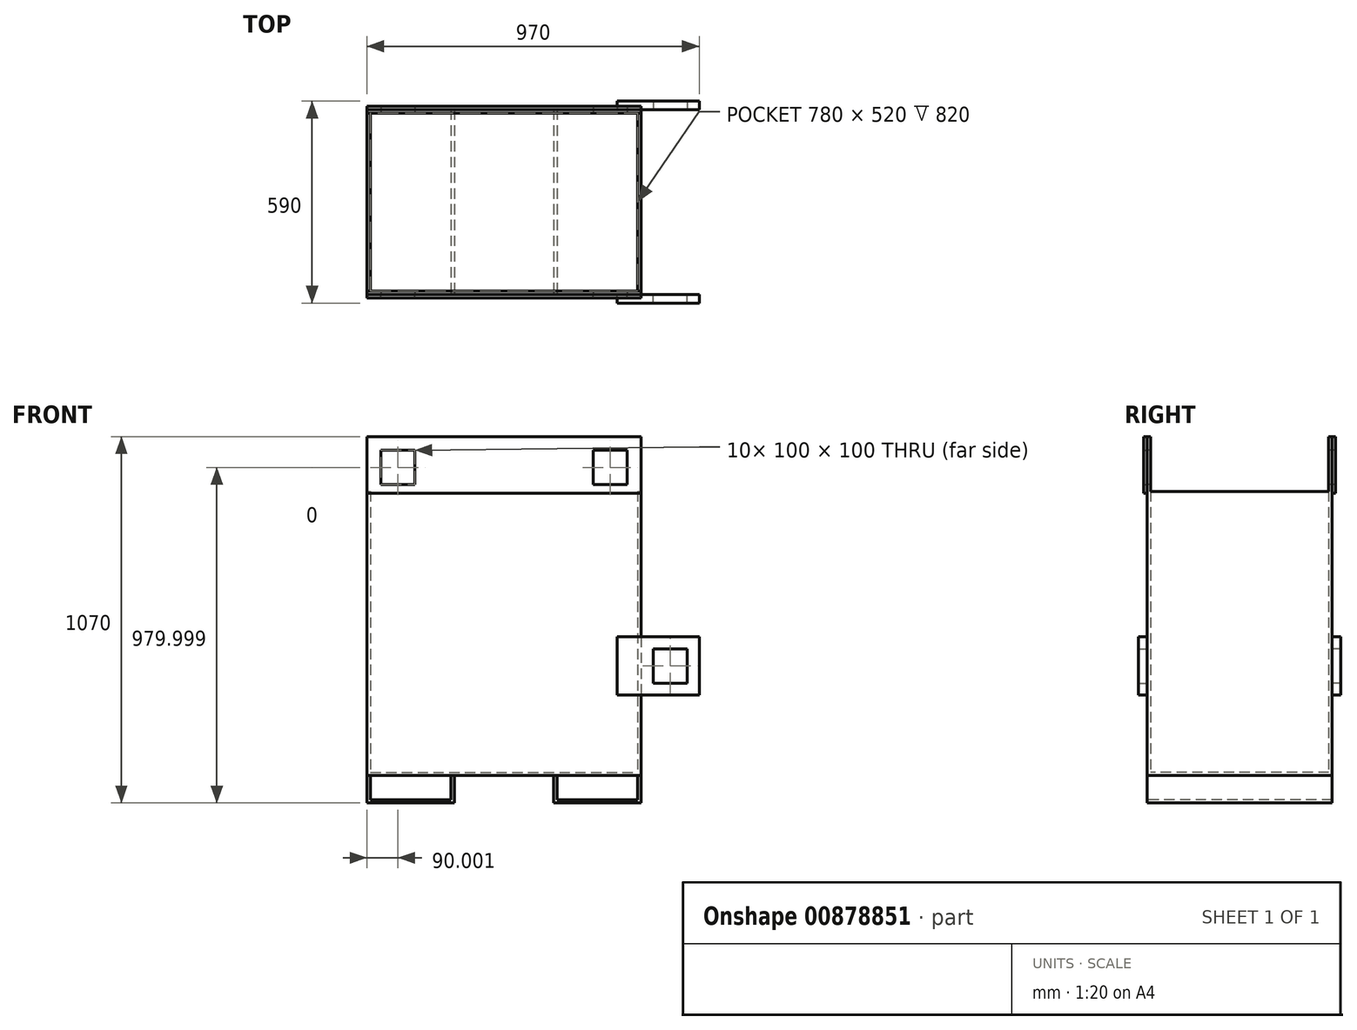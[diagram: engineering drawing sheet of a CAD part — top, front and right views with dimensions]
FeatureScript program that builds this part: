
annotation { "Feature Type Name" : "Feature", "Feature Type Description" : "" }
export const myFeature = defineFeature(function(context is Context, id is Id, definition is map)
    precondition{}
    {
        {
            var Q0;
            Q0=qCreatedBy(makeId("Front.planeOp"),FACE);
            var sketch = newSketch(context, id + "F0", { "sketchPlane" : qUnion([Q0])});
            skLineSegment(sketch, "E0.bottom", {"start": v(-449.14, -487.23) * mm, "end": v(350.86, -487.23) * mm});
            skLineSegment(sketch, "E0.top", {"start": v(-449.14, -497.23) * mm, "end": v(350.86, -497.23) * mm});
            skLineSegment(sketch, "E0.left", {"start": v(-449.14, -487.23) * mm, "end": v(-449.14, -497.23) * mm});
            skLineSegment(sketch, "E0.right", {"start": v(350.86, -487.23) * mm, "end": v(350.86, -497.23) * mm});
            skSolve(sketch);
        }
        {
            var Q0;
            Q0=makeQuery(id+"F0.imprint","IMPRINT",FACE,{"disambiguationData":[TD([[makeQuery(id+"F0.imprint","IMPRINT",EDGE,{"derivedFrom":sQuery(id+"F0.wireOp",EDGE,"E0.bottom")}),-1.0]])]});
            extrude(context, id + "F1", {"entities" : qUnion([Q0]), "depth" : 540 * mm, "offsetDistance" : 25 * mm});
        }
        {
            var Q0;
            Q0=makeQuery(id+"F1.opExtrude","SWEPT_FACE",FACE,{"disambiguationData":[OSD([sQuery(id+"F0.wireOp",EDGE,"E0.bottom")])]});
            var sketch = newSketch(context, id + "F2", { "sketchPlane" : qUnion([Q0])});
            skLineSegment(sketch, "E1.bottom", {"start": v(-439.14, -10) * mm, "end": v(340.86, -10) * mm});
            skLineSegment(sketch, "E1.top", {"start": v(-439.14, -530) * mm, "end": v(340.86, -530) * mm});
            skLineSegment(sketch, "E1.left", {"start": v(-439.14, -10) * mm, "end": v(-439.14, -530) * mm});
            skLineSegment(sketch, "E1.right", {"start": v(340.86, -10) * mm, "end": v(340.86, -530) * mm});
            skLineSegment(sketch, "E2.0", {"start": v(-449.14, 0) * mm, "end": v(350.86, 0) * mm});
            skLineSegment(sketch, "E3.0", {"start": v(-449.14, -540) * mm, "end": v(-449.14, 0) * mm});
            skLineSegment(sketch, "E4.0", {"start": v(350.86, -540) * mm, "end": v(350.86, 0) * mm});
            skLineSegment(sketch, "E5.0", {"start": v(-449.14, -540) * mm, "end": v(350.86, -540) * mm});
            skSolve(sketch);
        }
        {
            var Q0;
            Q0=makeQuery(id+"F2.imprint","IMPRINT",FACE,{"disambiguationData":[TD([[makeQuery(id+"F2.imprint","IMPRINT",EDGE,{"derivedFrom":sQuery(id+"F2.wireOp",EDGE,"E1.bottom")}),1.0]])]});
            extrude(context, id + "F3", {"entities" : qUnion([Q0]), "operationType" : NewBodyOperationType.ADD, "depth" : 820 * mm, "offsetDistance" : 25 * mm});
        }
        {
            var Q0;
            Q0=makeQuery(id+"F3.opExtrude","CAP_FACE",FACE,{"disambiguationData":[OSD([sQuery(id+"F2.wireOp",EDGE,"E1.bottom"),sQuery(id+"F2.wireOp",EDGE,"E1.top"),sQuery(id+"F2.wireOp",EDGE,"E1.left"),sQuery(id+"F2.wireOp",EDGE,"E1.right"),sQuery(id+"F2.wireOp",EDGE,"E2.0"),sQuery(id+"F2.wireOp",EDGE,"E3.0"),sQuery(id+"F2.wireOp",EDGE,"E4.0"),sQuery(id+"F2.wireOp",EDGE,"E5.0")])],"isStart":false});
            var sketch = newSketch(context, id + "F4", { "sketchPlane" : qUnion([Q0])});
            skLineSegment(sketch, "E6.bottom", {"start": v(-449.14, 0) * mm, "end": v(350.86, 0) * mm});
            skLineSegment(sketch, "E6.top", {"start": v(-449.14, -10) * mm, "end": v(350.86, -10) * mm});
            skLineSegment(sketch, "E6.left", {"start": v(-449.14, 0) * mm, "end": v(-449.14, -10) * mm});
            skLineSegment(sketch, "E6.right", {"start": v(350.86, 0) * mm, "end": v(350.86, -10) * mm});
            skLineSegment(sketch, "E7.bottom", {"start": v(350.86, -540) * mm, "end": v(-449.14, -540) * mm});
            skLineSegment(sketch, "E7.top", {"start": v(350.86, -530) * mm, "end": v(-449.14, -530) * mm});
            skLineSegment(sketch, "E7.left", {"start": v(350.86, -540) * mm, "end": v(350.86, -530) * mm});
            skLineSegment(sketch, "E7.right", {"start": v(-449.14, -540) * mm, "end": v(-449.14, -530) * mm});
            skSolve(sketch);
        }
        {
            var Q0;
            Q0=makeQuery(id+"F4.imprint","IMPRINT",FACE,{"disambiguationData":[TD([[makeQuery(id+"F4.imprint","IMPRINT",EDGE,{"derivedFrom":sQuery(id+"F4.wireOp",EDGE,"E6.bottom")}),-1.0]])]});
            var Q1;
            Q1=makeQuery(id+"F4.imprint","IMPRINT",FACE,{"disambiguationData":[TD([[makeQuery(id+"F4.imprint","IMPRINT",EDGE,{"derivedFrom":sQuery(id+"F4.wireOp",EDGE,"E7.bottom")}),1.0]])]});
            extrude(context, id + "F5", {"entities" : qUnion([Q0, Q1]), "operationType" : NewBodyOperationType.ADD, "depth" : 160 * mm, "offsetDistance" : 25 * mm});
        }
        {
            var Q0;
            Q0=makeQuery(id+"F5.boolean.opBoolean","MERGE",FACE,{"derivedFrom":[makeQuery(id+"F3.boolean.opBoolean","MERGE",FACE,{"derivedFrom":[makeQuery(id+"F1.opExtrude","CAP_FACE",FACE,{"disambiguationData":[OSD([sQuery(id+"F0.wireOp",EDGE,"E0.bottom"),sQuery(id+"F0.wireOp",EDGE,"E0.top"),sQuery(id+"F0.wireOp",EDGE,"E0.left"),sQuery(id+"F0.wireOp",EDGE,"E0.right")])],"isStart":false}),makeQuery(id+"F3.opExtrude","SWEPT_FACE",FACE,{"disambiguationData":[OSD([sQuery(id+"F2.wireOp",EDGE,"E5.0")])]})]}),makeQuery(id+"F5.opExtrude","SWEPT_FACE",FACE,{"disambiguationData":[OSD([sQuery(id+"F4.wireOp",EDGE,"E7.bottom")])]})]});
            var sketch = newSketch(context, id + "F6", { "sketchPlane" : qUnion([Q0])});
            skLineSegment(sketch, "E8.bottom", {"start": v(-409.14, 452.77) * mm, "end": v(-309.14, 452.77) * mm});
            skLineSegment(sketch, "E8.top", {"start": v(-409.14, 352.77) * mm, "end": v(-309.14, 352.77) * mm});
            skLineSegment(sketch, "E8.left", {"start": v(-409.14, 452.77) * mm, "end": v(-409.14, 352.77) * mm});
            skLineSegment(sketch, "E8.right", {"start": v(-309.14, 452.77) * mm, "end": v(-309.14, 352.77) * mm});
            skLineSegment(sketch, "E9", {"start": v(-49.14, 492.77) * mm, "end": v(-49.14, 340.22) * mm});
            skLineSegment(sketch, "E10.MirrorCS", {"start": v(210.86, 452.77) * mm, "end": v(210.86, 352.77) * mm});
            skLineSegment(sketch, "E11.MirrorCS", {"start": v(310.86, 452.77) * mm, "end": v(210.86, 452.77) * mm});
            skLineSegment(sketch, "E12.MirrorCS", {"start": v(310.86, 452.77) * mm, "end": v(310.86, 352.77) * mm});
            skLineSegment(sketch, "E13.MirrorCS", {"start": v(310.86, 352.77) * mm, "end": v(210.86, 352.77) * mm});
            skSolve(sketch);
        }
        {
            var Q0;
            Q0=makeQuery(id+"F6.imprint","IMPRINT",FACE,{"disambiguationData":[TD([[makeQuery(id+"F6.imprint","IMPRINT",EDGE,{"derivedFrom":sQuery(id+"F6.wireOp",EDGE,"E8.bottom")}),-1.0]])]});
            var Q1;
            Q1=makeQuery(id+"F6.imprint","IMPRINT",FACE,{"disambiguationData":[TD([[makeQuery(id+"F6.imprint","IMPRINT",EDGE,{"derivedFrom":sQuery(id+"F6.wireOp",EDGE,"E10.MirrorCS")}),1.0]])]});
            extrude(context, id + "F7", {"entities" : qUnion([Q0, Q1]), "operationType" : NewBodyOperationType.REMOVE, "oppositeDirection" : true, "depth" : 918 * mm, "offsetDistance" : 25 * mm});
        }
        {
            var Q0;
            Q0=makeQuery(id+"F5.boolean.opBoolean","MERGE",FACE,{"derivedFrom":[makeQuery(id+"F3.boolean.opBoolean","MERGE",FACE,{"derivedFrom":[makeQuery(id+"F1.opExtrude","CAP_FACE",FACE,{"disambiguationData":[OSD([sQuery(id+"F0.wireOp",EDGE,"E0.bottom"),sQuery(id+"F0.wireOp",EDGE,"E0.top"),sQuery(id+"F0.wireOp",EDGE,"E0.left"),sQuery(id+"F0.wireOp",EDGE,"E0.right")])],"isStart":false}),makeQuery(id+"F3.opExtrude","SWEPT_FACE",FACE,{"disambiguationData":[OSD([sQuery(id+"F2.wireOp",EDGE,"E5.0")])]})]}),makeQuery(id+"F5.opExtrude","SWEPT_FACE",FACE,{"disambiguationData":[OSD([sQuery(id+"F4.wireOp",EDGE,"E7.bottom")])]})]});
            var sketch = newSketch(context, id + "F8", { "sketchPlane" : qUnion([Q0])});
            skLineSegment(sketch, "E14.bottom", {"start": v(-449.14, 492.77) * mm, "end": v(350.86, 492.77) * mm});
            skLineSegment(sketch, "E14.top", {"start": v(-449.14, 327.77) * mm, "end": v(350.86, 327.77) * mm});
            skLineSegment(sketch, "E14.left", {"start": v(-449.14, 492.77) * mm, "end": v(-449.14, 327.77) * mm});
            skLineSegment(sketch, "E14.right", {"start": v(350.86, 492.77) * mm, "end": v(350.86, 327.77) * mm});
            skSolve(sketch);
        }
        {
            var Q0;
            Q0=makeQuery(id+"F8.imprint","IMPRINT",FACE,{"disambiguationData":[TD([[makeQuery(id+"F8.imprint","IMPRINT",EDGE,{"derivedFrom":sQuery(id+"F8.wireOp",EDGE,"E14.bottom")}),-1.0]])]});
            extrude(context, id + "F9", {"entities" : qUnion([Q0]), "depth" : 10 * mm, "offsetDistance" : 25 * mm});
        }
        {
            var Q0;
            Q0=makeQuery(id+"F5.boolean.opBoolean","MERGE",FACE,{"derivedFrom":[makeQuery(id+"F3.boolean.opBoolean","MERGE",FACE,{"derivedFrom":[makeQuery(id+"F1.opExtrude","CAP_FACE",FACE,{"disambiguationData":[OSD([sQuery(id+"F0.wireOp",EDGE,"E0.bottom"),sQuery(id+"F0.wireOp",EDGE,"E0.top"),sQuery(id+"F0.wireOp",EDGE,"E0.left"),sQuery(id+"F0.wireOp",EDGE,"E0.right")])],"isStart":true}),makeQuery(id+"F3.opExtrude","SWEPT_FACE",FACE,{"disambiguationData":[OSD([sQuery(id+"F2.wireOp",EDGE,"E2.0")])]})]}),makeQuery(id+"F5.opExtrude","SWEPT_FACE",FACE,{"disambiguationData":[OSD([sQuery(id+"F4.wireOp",EDGE,"E6.bottom")])]})]});
            var sketch = newSketch(context, id + "F10", { "sketchPlane" : qUnion([Q0])});
            skLineSegment(sketch, "E15.bottom", {"start": v(-350.86, 492.77) * mm, "end": v(449.14, 492.77) * mm});
            skLineSegment(sketch, "E15.top", {"start": v(-350.86, 327.77) * mm, "end": v(449.14, 327.77) * mm});
            skLineSegment(sketch, "E15.left", {"start": v(-350.86, 492.77) * mm, "end": v(-350.86, 327.77) * mm});
            skLineSegment(sketch, "E15.right", {"start": v(449.14, 492.77) * mm, "end": v(449.14, 327.77) * mm});
            skSolve(sketch);
        }
        {
            var Q0;
            Q0=makeQuery(id+"F10.imprint","IMPRINT",FACE,{"disambiguationData":[TD([[makeQuery(id+"F10.imprint","IMPRINT",EDGE,{"derivedFrom":sQuery(id+"F10.wireOp",EDGE,"E15.bottom")}),1.0]])]});
            extrude(context, id + "F11", {"entities" : qUnion([Q0]), "depth" : 10 * mm, "offsetDistance" : 25 * mm});
        }
        {
            var Q0;
            Q0=makeQuery(id+"F5.boolean.opBoolean","MERGE",FACE,{"derivedFrom":[makeQuery(id+"F3.boolean.opBoolean","MERGE",FACE,{"derivedFrom":[makeQuery(id+"F1.opExtrude","CAP_FACE",FACE,{"disambiguationData":[OSD([sQuery(id+"F0.wireOp",EDGE,"E0.bottom"),sQuery(id+"F0.wireOp",EDGE,"E0.top"),sQuery(id+"F0.wireOp",EDGE,"E0.left"),sQuery(id+"F0.wireOp",EDGE,"E0.right")])],"isStart":false}),makeQuery(id+"F3.opExtrude","SWEPT_FACE",FACE,{"disambiguationData":[OSD([sQuery(id+"F2.wireOp",EDGE,"E5.0")])]})]}),makeQuery(id+"F5.opExtrude","SWEPT_FACE",FACE,{"disambiguationData":[OSD([sQuery(id+"F4.wireOp",EDGE,"E7.bottom")])]})]});
            var sketch = newSketch(context, id + "F12", { "sketchPlane" : qUnion([Q0])});
            skLineSegment(sketch, "E16.bottom", {"start": v(-449.14, -497.23) * mm, "end": v(-194.14, -497.23) * mm});
            skLineSegment(sketch, "E16.top", {"start": v(-449.14, -577.23) * mm, "end": v(-194.14, -577.23) * mm});
            skLineSegment(sketch, "E16.left", {"start": v(-449.14, -497.23) * mm, "end": v(-449.14, -577.23) * mm});
            skLineSegment(sketch, "E16.right", {"start": v(-194.14, -497.23) * mm, "end": v(-194.14, -577.23) * mm});
            skLineSegment(sketch, "E17", {"start": v(-49.14, -497.23) * mm, "end": v(-49.14, -332.02) * mm});
            skLineSegment(sketch, "E18.MirrorCS", {"start": v(350.86, -577.23) * mm, "end": v(95.86, -577.23) * mm});
            skLineSegment(sketch, "E19.MirrorCS", {"start": v(350.86, -497.23) * mm, "end": v(350.86, -577.23) * mm});
            skLineSegment(sketch, "E20.MirrorCS", {"start": v(95.86, -497.23) * mm, "end": v(95.86, -577.23) * mm});
            skLineSegment(sketch, "E21.MirrorCS", {"start": v(350.86, -497.23) * mm, "end": v(95.86, -497.23) * mm});
            skLineSegment(sketch, "E22.bottom", {"start": v(-439.14, -497.23) * mm, "end": v(-204.14, -497.23) * mm});
            skLineSegment(sketch, "E22.top", {"start": v(-439.14, -567.23) * mm, "end": v(-204.14, -567.23) * mm});
            skLineSegment(sketch, "E22.left", {"start": v(-439.14, -497.23) * mm, "end": v(-439.14, -567.23) * mm});
            skLineSegment(sketch, "E22.right", {"start": v(-204.14, -497.23) * mm, "end": v(-204.14, -567.23) * mm});
            skLineSegment(sketch, "E23.MirrorCS", {"start": v(105.86, -497.23) * mm, "end": v(105.86, -567.23) * mm});
            skLineSegment(sketch, "E24.MirrorCS", {"start": v(340.86, -567.23) * mm, "end": v(105.86, -567.23) * mm});
            skLineSegment(sketch, "E25.MirrorCS", {"start": v(340.86, -497.23) * mm, "end": v(340.86, -567.23) * mm});
            skLineSegment(sketch, "E26.MirrorCS", {"start": v(340.86, -497.23) * mm, "end": v(105.86, -497.23) * mm});
            skSolve(sketch);
        }
        {
            var Q0;
            Q0=makeQuery(id+"F12.imprint","IMPRINT",FACE,{"disambiguationData":[TD([[makeQuery(id+"F12.imprint","IMPRINT",EDGE,{"derivedFrom":sQuery(id+"F12.wireOp",EDGE,"E16.top")}),1.0]])]});
            var Q1;
            Q1=makeQuery(id+"F12.imprint","IMPRINT",FACE,{"disambiguationData":[TD([[makeQuery(id+"F12.imprint","IMPRINT",EDGE,{"derivedFrom":sQuery(id+"F12.wireOp",EDGE,"E18.MirrorCS")}),-1.0]])]});
            var Q2;
            Q2=makeQuery(id+"F5.boolean.opBoolean","MERGE",FACE,{"derivedFrom":[makeQuery(id+"F3.boolean.opBoolean","MERGE",FACE,{"derivedFrom":[makeQuery(id+"F1.opExtrude","CAP_FACE",FACE,{"disambiguationData":[OSD([sQuery(id+"F0.wireOp",EDGE,"E0.bottom"),sQuery(id+"F0.wireOp",EDGE,"E0.top"),sQuery(id+"F0.wireOp",EDGE,"E0.left"),sQuery(id+"F0.wireOp",EDGE,"E0.right")])],"isStart":true}),makeQuery(id+"F3.opExtrude","SWEPT_FACE",FACE,{"disambiguationData":[OSD([sQuery(id+"F2.wireOp",EDGE,"E2.0")])]})]}),makeQuery(id+"F5.opExtrude","SWEPT_FACE",FACE,{"disambiguationData":[OSD([sQuery(id+"F4.wireOp",EDGE,"E6.bottom")])]})]});
            extrude(context, id + "F13", {"entities" : qUnion([Q0, Q1]), "endBound" : BoundingType.UP_TO_SURFACE, "oppositeDirection" : true, "depth" : 654 * mm, "endBoundEntityFace" : qUnion([Q2]), "offsetDistance" : 25 * mm});
        }
        {
            var Q0;
            Q0=makeQuery(id+"F5.boolean.opBoolean","MERGE",FACE,{"derivedFrom":[makeQuery(id+"F3.boolean.opBoolean","MERGE",FACE,{"derivedFrom":[makeQuery(id+"F1.opExtrude","CAP_FACE",FACE,{"disambiguationData":[OSD([sQuery(id+"F0.wireOp",EDGE,"E0.bottom"),sQuery(id+"F0.wireOp",EDGE,"E0.top"),sQuery(id+"F0.wireOp",EDGE,"E0.left"),sQuery(id+"F0.wireOp",EDGE,"E0.right")])],"isStart":true}),makeQuery(id+"F3.opExtrude","SWEPT_FACE",FACE,{"disambiguationData":[OSD([sQuery(id+"F2.wireOp",EDGE,"E2.0")])]})]}),makeQuery(id+"F5.opExtrude","SWEPT_FACE",FACE,{"disambiguationData":[OSD([sQuery(id+"F4.wireOp",EDGE,"E6.bottom")])]})]});
            var sketch = newSketch(context, id + "F14", { "sketchPlane" : qUnion([Q0])});
            skLineSegment(sketch, "E27", {"start": v(-350.86, -497.23) * mm, "end": v(-350.86, -262.23) * mm});
            skLineSegment(sketch, "E28", {"start": v(-350.86, -262.23) * mm, "end": v(-520.86, -262.23) * mm});
            skLineSegment(sketch, "E29", {"start": v(-520.86, -262.23) * mm, "end": v(-520.86, -92.23) * mm});
            skLineSegment(sketch, "E30", {"start": v(-520.86, -92.23) * mm, "end": v(-350.86, -92.23) * mm});
            skLineSegment(sketch, "E31", {"start": v(-350.86, -92.23) * mm, "end": v(-280.86, -92.23) * mm});
            skLineSegment(sketch, "E32", {"start": v(-280.86, -92.23) * mm, "end": v(-280.86, -262.23) * mm});
            skLineSegment(sketch, "E33", {"start": v(-280.86, -262.23) * mm, "end": v(-350.86, -262.23) * mm});
            skLineSegment(sketch, "E34", {"start": v(-435.86, -92.23) * mm, "end": v(-435.86, -177.23) * mm});
            skPoint(sketch, "E34.endSnap0", {"position": v(-520.86, -177.23) * mm});
            skLineSegment(sketch, "E35", {"start": v(-435.86, -177.23) * mm, "end": v(-485.86, -177.23) * mm});
            skLineSegment(sketch, "E36", {"start": v(-485.86, -177.23) * mm, "end": v(-485.86, -227.23) * mm});
            skLineSegment(sketch, "E37.MirrorCS", {"start": v(-385.86, -177.23) * mm, "end": v(-385.86, -227.23) * mm});
            skLineSegment(sketch, "E38", {"start": v(-485.86, -227.23) * mm, "end": v(-385.86, -227.23) * mm});
            skLineSegment(sketch, "E39.MirrorCS", {"start": v(-485.86, -127.23) * mm, "end": v(-385.86, -127.23) * mm});
            skLineSegment(sketch, "E40.MirrorCS", {"start": v(-485.86, -177.23) * mm, "end": v(-485.86, -127.23) * mm});
            skLineSegment(sketch, "E41.MirrorCS", {"start": v(-385.86, -177.23) * mm, "end": v(-385.86, -127.23) * mm});
            skSolve(sketch);
        }
        {
            var Q0;
            {var subQ0=sQuery(id+"F14.wireOp",EDGE,"E28");Q0=makeQuery(id+"F14.imprint","IMPRINT",FACE,{"disambiguationData":[TD([[makeQuery(id+"F14.imprint","IMPRINT",EDGE,{"derivedFrom":subQ0}),-1.0]])]});}
            var Q1;
            {var subQ0=sQuery(id+"F14.wireOp",EDGE,"E31");Q1=makeQuery(id+"F14.imprint","IMPRINT",FACE,{"disambiguationData":[TD([[makeQuery(id+"F14.imprint","IMPRINT",EDGE,{"derivedFrom":subQ0}),-1.0]])]});}
            extrude(context, id + "F15", {"entities" : qUnion([Q0, Q1]), "depth" : 25 * mm, "offsetDistance" : 25 * mm});
        }
        {
            var Q0;
            Q0=makeQuery(id+"F5.boolean.opBoolean","MERGE",FACE,{"derivedFrom":[makeQuery(id+"F3.boolean.opBoolean","MERGE",FACE,{"derivedFrom":[makeQuery(id+"F1.opExtrude","CAP_FACE",FACE,{"disambiguationData":[OSD([sQuery(id+"F0.wireOp",EDGE,"E0.bottom"),sQuery(id+"F0.wireOp",EDGE,"E0.top"),sQuery(id+"F0.wireOp",EDGE,"E0.left"),sQuery(id+"F0.wireOp",EDGE,"E0.right")])],"isStart":false}),makeQuery(id+"F3.opExtrude","SWEPT_FACE",FACE,{"disambiguationData":[OSD([sQuery(id+"F2.wireOp",EDGE,"E5.0")])]})]}),makeQuery(id+"F5.opExtrude","SWEPT_FACE",FACE,{"disambiguationData":[OSD([sQuery(id+"F4.wireOp",EDGE,"E7.bottom")])]})]});
            var sketch = newSketch(context, id + "F16", { "sketchPlane" : qUnion([Q0])});
            skLineSegment(sketch, "E42.0.0", {"start": v(520.86, -92.23) * mm, "end": v(280.86, -92.23) * mm});
            skLineSegment(sketch, "E42.0.1", {"start": v(280.86, -92.23) * mm, "end": v(280.86, -262.23) * mm});
            skLineSegment(sketch, "E42.0.2", {"start": v(280.86, -262.23) * mm, "end": v(520.86, -262.23) * mm});
            skLineSegment(sketch, "E42.0.3", {"start": v(520.86, -262.23) * mm, "end": v(520.86, -92.23) * mm});
            skLineSegment(sketch, "E43.0", {"start": v(485.86, -127.23) * mm, "end": v(385.86, -127.23) * mm});
            skLineSegment(sketch, "E44.0", {"start": v(385.86, -227.23) * mm, "end": v(385.86, -127.23) * mm});
            skLineSegment(sketch, "E45.0", {"start": v(485.86, -127.23) * mm, "end": v(485.86, -227.23) * mm});
            skLineSegment(sketch, "E46.0", {"start": v(485.86, -227.23) * mm, "end": v(385.86, -227.23) * mm});
            skSolve(sketch);
        }
        {
            var Q0;
            {var subQ0=sQuery(id+"F16.wireOp",EDGE,"E42.0.1");Q0=makeQuery(id+"F16.imprint","IMPRINT",FACE,{"disambiguationData":[TD([[makeQuery(id+"F16.imprint","IMPRINT",EDGE,{"derivedFrom":subQ0}),1.0]])]});}
            var Q1;
            {var subQ0=sQuery(id+"F16.wireOp",EDGE,"E42.0.3");Q1=makeQuery(id+"F16.imprint","IMPRINT",FACE,{"disambiguationData":[TD([[makeQuery(id+"F16.imprint","IMPRINT",EDGE,{"derivedFrom":subQ0}),1.0]])]});}
            extrude(context, id + "F17", {"entities" : qUnion([Q0, Q1]), "depth" : 25 * mm, "offsetDistance" : 25 * mm});
        }
    });
